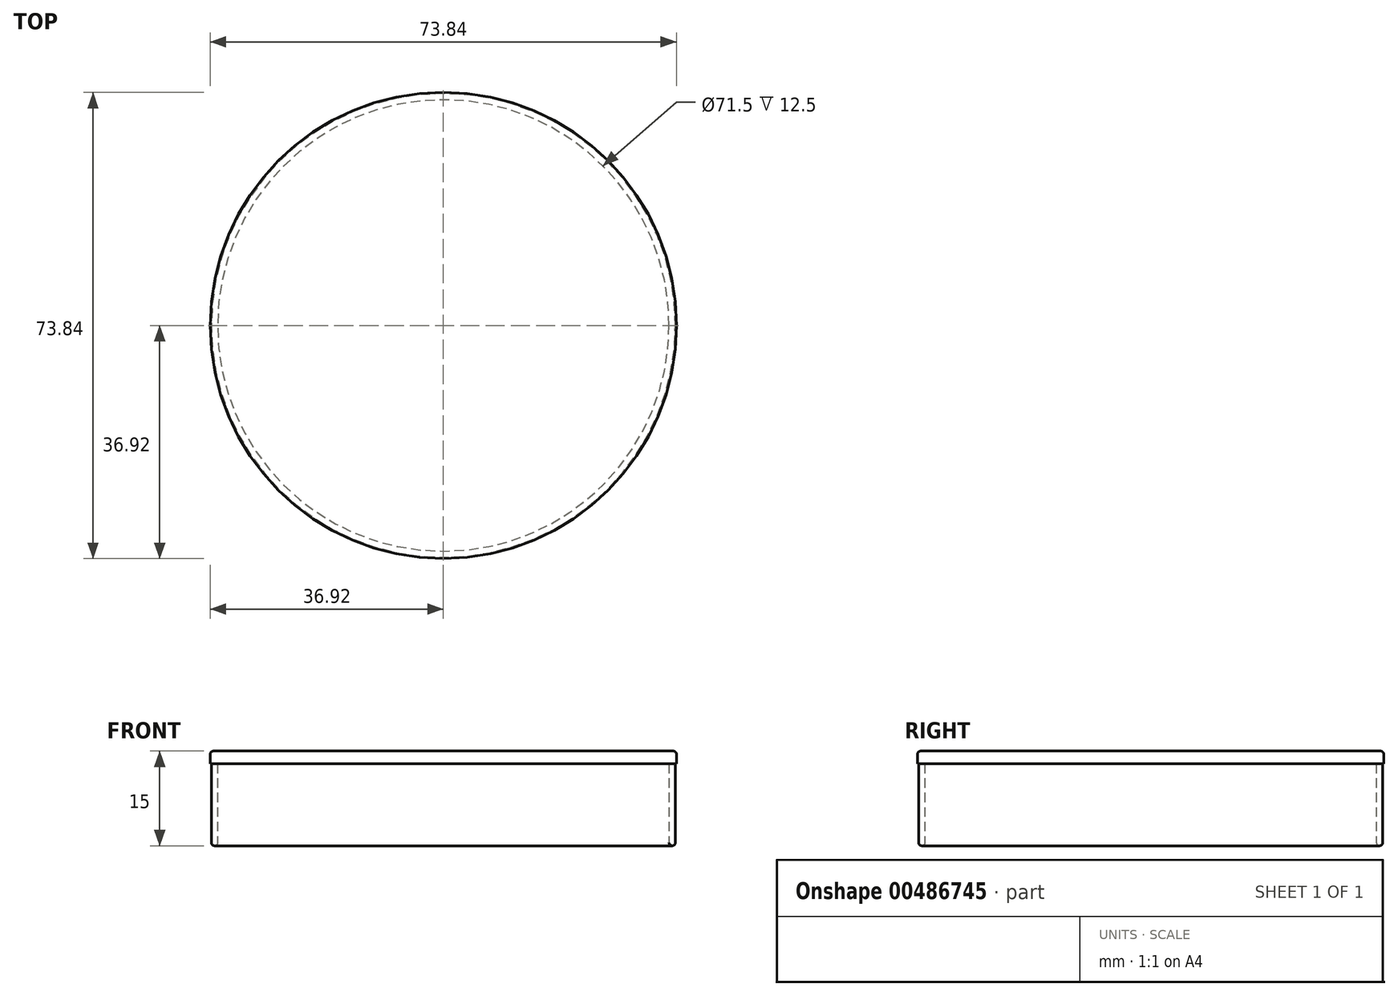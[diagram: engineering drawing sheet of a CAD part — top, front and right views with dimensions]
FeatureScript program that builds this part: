
annotation { "Feature Type Name" : "Feature", "Feature Type Description" : "" }
export const myFeature = defineFeature(function(context is Context, id is Id, definition is map)
    precondition{}
    {
        {
            var Q0;
            Q0=qCreatedBy(makeId("Top.planeOp"),FACE);
            var sketch = newSketch(context, id + "F0", { "sketchPlane" : qUnion([Q0])});
            skCircle(sketch, "E0", {"center": v(0, 0) * mm, "radius": 35.75 * mm});
            skCircle(sketch, "E1.0", {"center": v(0, 0) * mm, "radius": 36.75 * mm});
            skSolve(sketch);
        }
        {
            var Q0;
            Q0=qSketchRegion(id+"F0",true);
            extrude(context, id + "F1", {"entities" : qUnion([Q0]), "depth" : 15 * mm});
        }
        {
            var Q0;
            Q0=makeQuery(id+"F1.opExtrude","CAP_FACE",FACE,{"disambiguationData":[OSD([sQuery(id+"F0.wireOp",EDGE,"E0"),sQuery(id+"F0.wireOp",EDGE,"E1.0")])],"isStart":false});
            var sketch = newSketch(context, id + "F2", { "sketchPlane" : qUnion([Q0])});
            skCircle(sketch, "E2", {"center": v(0, 0) * mm, "radius": 36.92 * mm});
            skSolve(sketch);
        }
        {
            var Q0;
            Q0=qSketchRegion(id+"F2",true);
            extrude(context, id + "F3", {"entities" : qUnion([Q0]), "operationType" : NewBodyOperationType.ADD, "oppositeDirection" : true, "depth" : 2 * mm});
        }
        {
            var Q0;
            Q0=makeQuery(id+"F1.opExtrude","CAP_FACE",FACE,{"disambiguationData":[OSD([sQuery(id+"F0.wireOp",EDGE,"E0"),sQuery(id+"F0.wireOp",EDGE,"E1.0")])],"isStart":true});
            var Q1;
            Q1=makeQuery(id+"F3.boolean.opBoolean","MERGE",FACE,{"derivedFrom":[makeQuery(id+"F1.opExtrude","CAP_FACE",FACE,{"disambiguationData":[OSD([sQuery(id+"F0.wireOp",EDGE,"E0"),sQuery(id+"F0.wireOp",EDGE,"E1.0")])],"isStart":false}),makeQuery(id+"F3.opExtrude","CAP_FACE",FACE,{"disambiguationData":[OSD([sQuery(id+"F2.wireOp",EDGE,"E2")])],"isStart":true})]});
            fillet(context, id + "F4", {"entities" : qUnion([Q0, Q1]), "radius" : .5 * mm, "tangentPropagation" : true, "allowEdgeOverflow" : false});
        }
    });
